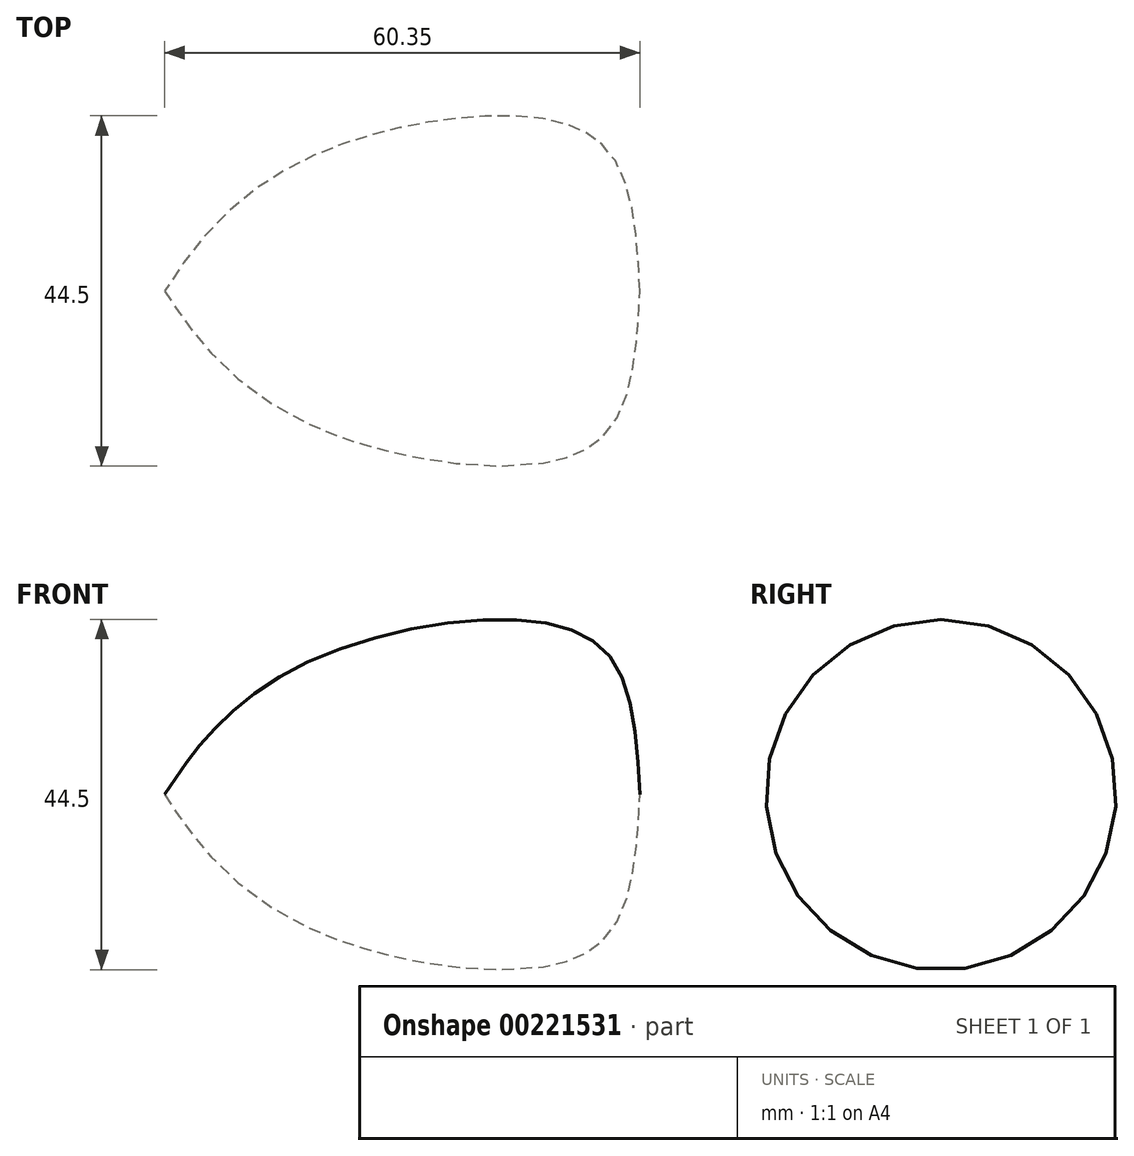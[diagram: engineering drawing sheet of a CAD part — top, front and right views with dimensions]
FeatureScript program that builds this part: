
annotation { "Feature Type Name" : "Feature", "Feature Type Description" : "" }
export const myFeature = defineFeature(function(context is Context, id is Id, definition is map)
    precondition{}
    {
        {
            var Q0;
            Q0=qCreatedBy(makeId("Front.planeOp"),FACE);
            var sketch = newSketch(context, id + "F0", { "sketchPlane" : qUnion([Q0])});
            skLineSegment(sketch, "E0", {"start": v(-67.25, 0) * mm, "end": v(71.56, 0) * mm});
            skFitSpline(sketch, "E1", {"points": [v(0, 0) * mm, v(5.17, 7.11) * mm, v(18.54, 17.03) * mm, v(44.83, 22.2) * mm, v(56.9, 17.03) * mm, v(60.35, 0) * mm], "startDerivative": vector(30.34, 46.9) * mm, "endDerivative": vector(5.16, -94.23) * mm});
            skLineSegment(sketch, "E2", {"start": v(60.35, 0) * mm, "end": v(0, 0) * mm});
            skSolve(sketch);
        }
        {
            var Q0;
            Q0=makeQuery(id+"F0.imprint","IMPRINT",FACE,{"disambiguationData":[TD([[makeQuery(id+"F0.imprint","IMPRINT",EDGE,{"derivedFrom":sQuery(id+"F0.wireOp",EDGE,"E1")}),-1.0]])]});
            var Q1;
            Q1=sQuery(id+"F0.wireOp",EDGE,"E0");
            revolve(context, id + "F1", {"entities" : qUnion([Q0]), "axis" : qUnion([Q1]), "revolveType" : RevolveType.FULL});
        }
    });
